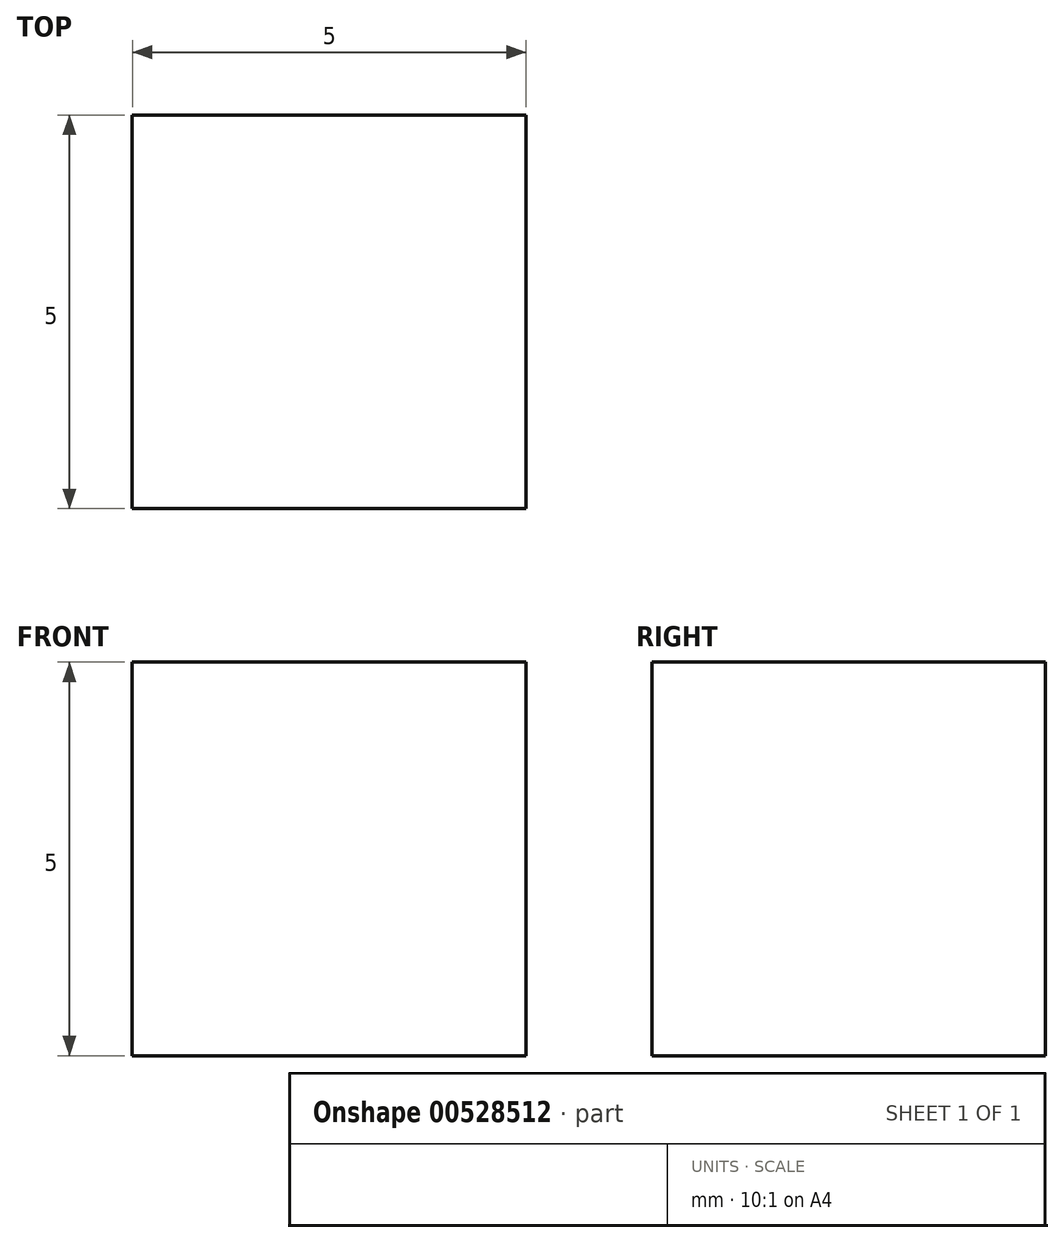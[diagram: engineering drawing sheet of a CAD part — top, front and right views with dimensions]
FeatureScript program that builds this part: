
annotation { "Feature Type Name" : "Feature", "Feature Type Description" : "" }
export const myFeature = defineFeature(function(context is Context, id is Id, definition is map)
    precondition{}
    {
        {
            var Q0;
            Q0=qCreatedBy(makeId("Top.planeOp"),FACE);
            var sketch = newSketch(context, id + "F0", { "sketchPlane" : qUnion([Q0])});
            skLineSegment(sketch, "E0.bottom", {"start": v(2.49, -2.5) * mm, "end": v(-2.51, -2.5) * mm});
            skLineSegment(sketch, "E0.top", {"start": v(2.49, 2.5) * mm, "end": v(-2.51, 2.5) * mm});
            skLineSegment(sketch, "E0.left", {"start": v(2.49, -2.5) * mm, "end": v(2.49, 2.5) * mm});
            skLineSegment(sketch, "E0.right", {"start": v(-2.51, -2.5) * mm, "end": v(-2.51, 2.5) * mm});
            skSolve(sketch);
        }
        {
            var Q0;
            Q0 = qSketchRegion(id + "F0", true);
            extrude(context, id + "F1", {"entities" : qUnion([Q0]), "depth" : 5 * mm, "offsetDistance" : 25 * mm});
        }
    });
